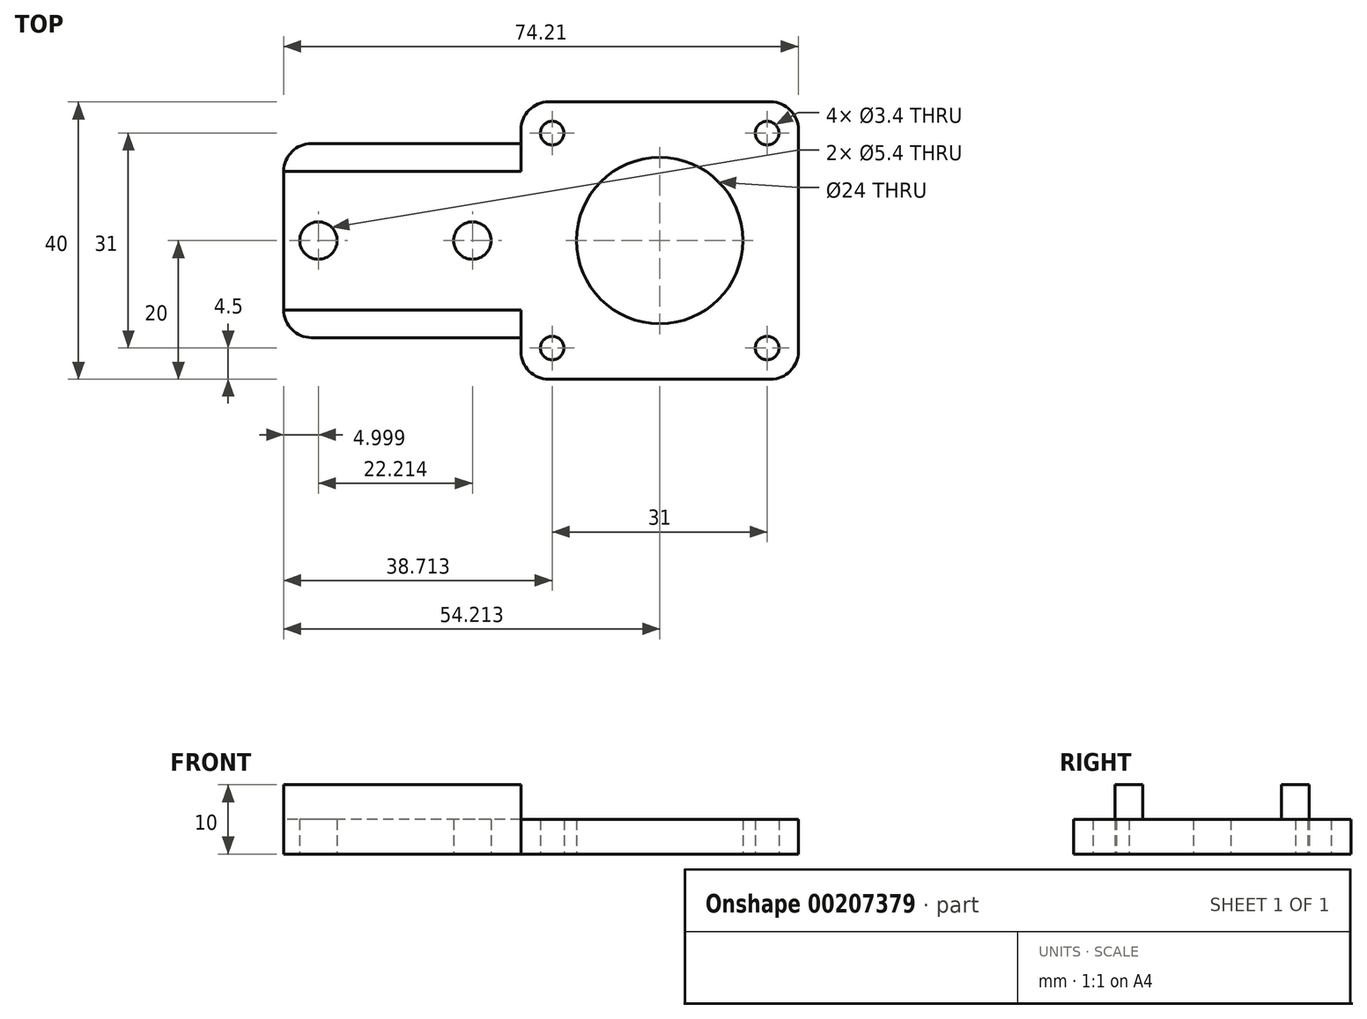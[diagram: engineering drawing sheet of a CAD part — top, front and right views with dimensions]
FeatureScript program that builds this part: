
annotation { "Feature Type Name" : "Feature", "Feature Type Description" : "" }
export const myFeature = defineFeature(function(context is Context, id is Id, definition is map)
    precondition{}
    {
        {
            var Q0;
            Q0=qCreatedBy(makeId("Top.planeOp"),FACE);
            var sketch = newSketch(context, id + "F0", { "sketchPlane" : qUnion([Q0])});
            skLineSegment(sketch, "E0.bottom", {"start": v(-6.6, -40) * mm, "end": v(-46.6, -40) * mm});
            skLineSegment(sketch, "E0.top", {"start": v(-6.6, 0) * mm, "end": v(-46.6, 0) * mm});
            skLineSegment(sketch, "E0.left", {"start": v(-6.6, -40) * mm, "end": v(-6.6, 0) * mm});
            skLineSegment(sketch, "E0.right", {"start": v(-46.6, -40) * mm, "end": v(-46.6, 0) * mm});
            skCircle(sketch, "E1", {"center": v(-42.1, -4.5) * mm, "radius": 1.7 * mm});
            skCircle(sketch, "E2", {"center": v(-42.1, -35.5) * mm, "radius": 1.7 * mm});
            skCircle(sketch, "E3", {"center": v(-11.1, -35.5) * mm, "radius": 1.7 * mm});
            skLineSegment(sketch, "E4", {"start": v(-42.1, -4.5) * mm, "end": v(-11.1, -35.5) * mm, "construction": true});
            skCircle(sketch, "E5", {"center": v(-26.6, -20) * mm, "radius": 12 * mm});
            skLineSegment(sketch, "E6", {"start": v(-46.6, -10) * mm, "end": v(-80.81, -10) * mm});
            skLineSegment(sketch, "E7", {"start": v(-80.81, -10) * mm, "end": v(-80.81, -30) * mm});
            skLineSegment(sketch, "E8", {"start": v(-80.81, -30) * mm, "end": v(-46.6, -30) * mm});
            skLineSegment(sketch, "E9", {"start": v(-46.6, -34) * mm, "end": v(-80.81, -34) * mm});
            skLineSegment(sketch, "E10", {"start": v(-80.81, -34) * mm, "end": v(-80.81, -30) * mm});
            skLineSegment(sketch, "E11", {"start": v(-46.6, -6) * mm, "end": v(-80.81, -6) * mm});
            skLineSegment(sketch, "E12", {"start": v(-80.81, -6) * mm, "end": v(-80.81, -10) * mm});
            skPoint(sketch, "E13", {"position": v(-80.81, -20) * mm});
            skCircle(sketch, "E14", {"center": v(-75.81, -20) * mm, "radius": 2.7 * mm});
            skCircle(sketch, "E15", {"center": v(-53.6, -20) * mm, "radius": 2.7 * mm});
            skPoint(sketch, "E16", {"position": v(-75.81, -6) * mm});
            skPoint(sketch, "E17", {"position": v(-53.6, -6) * mm});
            skCircle(sketch, "E18", {"center": v(-11.1, -4.5) * mm, "radius": 1.7 * mm});
            skSolve(sketch);
        }
        {
            var Q0;
            {var subQ1=sQuery(id+"F0.wireOp",EDGE,"E6");Q0=makeQuery(id+"F0.imprint","IMPRINT",FACE,{"disambiguationData":[TD([[makeQuery(id+"F0.imprint","IMPRINT",EDGE,{"derivedFrom":subQ1}),1.0]])]});}
            var Q1;
            {var subQ5=sQuery(id+"F0.wireOp",EDGE,"E0.bottom");Q1=makeQuery(id+"F0.imprint","IMPRINT",FACE,{"disambiguationData":[TD([[makeQuery(id+"F0.imprint","IMPRINT",EDGE,{"derivedFrom":subQ5}),-1.0]])]});}
            extrude(context, id + "F1", {"entities" : qUnion([Q0, Q1]), "depth" : 5 * mm});
        }
        {
            var Q0;
            {var subQ1=sQuery(id+"F0.wireOp",EDGE,"E6");Q0=makeQuery(id+"F0.imprint","IMPRINT",FACE,{"disambiguationData":[TD([[makeQuery(id+"F0.imprint","IMPRINT",EDGE,{"derivedFrom":subQ1}),-1.0]])]});}
            var Q1;
            {var subQ1=sQuery(id+"F0.wireOp",EDGE,"E8");Q1=makeQuery(id+"F0.imprint","IMPRINT",FACE,{"disambiguationData":[TD([[makeQuery(id+"F0.imprint","IMPRINT",EDGE,{"derivedFrom":subQ1}),-1.0]])]});}
            extrude(context, id + "F2", {"entities" : qUnion([Q0, Q1]), "operationType" : NewBodyOperationType.ADD, "depth" : 10 * mm});
        }
        {
            var Q0;
            Q0=makeQuery(id+"F2.opExtrude","SWEPT_EDGE",EDGE,{"disambiguationData":[OSD([sQuery(id+"F0.wireOp",EDGE,"E11"),sQuery(id+"F0.wireOp",EDGE,"E12")])]});
            var Q1;
            Q1=makeQuery(id+"F1.opExtrude","SWEPT_EDGE",EDGE,{"disambiguationData":[OSD([sQuery(id+"F0.wireOp",EDGE,"E0.top"),sQuery(id+"F0.wireOp",EDGE,"E0.right")])]});
            var Q2;
            Q2=makeQuery(id+"F1.opExtrude","SWEPT_EDGE",EDGE,{"disambiguationData":[OSD([sQuery(id+"F0.wireOp",EDGE,"E0.top"),sQuery(id+"F0.wireOp",EDGE,"E0.left")])]});
            var Q3;
            Q3=makeQuery(id+"F1.opExtrude","SWEPT_EDGE",EDGE,{"disambiguationData":[OSD([sQuery(id+"F0.wireOp",EDGE,"E0.bottom"),sQuery(id+"F0.wireOp",EDGE,"E0.left")])]});
            var Q4;
            Q4=makeQuery(id+"F1.opExtrude","SWEPT_EDGE",EDGE,{"disambiguationData":[OSD([sQuery(id+"F0.wireOp",EDGE,"E0.bottom"),sQuery(id+"F0.wireOp",EDGE,"E0.right")])]});
            var Q5;
            Q5=makeQuery(id+"F2.opExtrude","SWEPT_EDGE",EDGE,{"disambiguationData":[OSD([sQuery(id+"F0.wireOp",EDGE,"E9"),sQuery(id+"F0.wireOp",EDGE,"E10")])]});
            fillet(context, id + "F3", {"entities" : qUnion([Q0, Q1, Q2, Q3, Q4, Q5]), "radius" : 4 * mm, "tangentPropagation" : true, "allowEdgeOverflow" : false});
        }
    });
